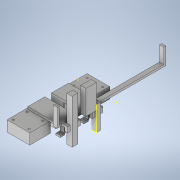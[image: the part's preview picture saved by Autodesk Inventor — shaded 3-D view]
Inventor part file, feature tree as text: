
AUTODESK INVENTOR PART (.ipt)
format: ipt  version: 2020.2 (Build 242310000, 310)  size: 1,098,752 bytes
history: native  units: mm
features: sketch x48, extrude x44, projected_geometry x21, hole x3, plane x1
ambient origin geometry x8: Origin, YZ Plane, XZ Plane, XY Plane, X Axis, Y Axis, Z Axis, Center Point
bodies: Solid1 (feature_tree)
feature tree (117):
  sketch  "Sketch1"  dims[d0=8.0mm d1=98.298mm]
  extrude  "Extrusion1"  Depth=98.298mm
  extrude  "Extrusion2"  Depth=4.0mm
  extrude  "Extrusion3"  Depth=4.0mm TaperAngle=0.0deg
  extrude  "Extrusion4"  Depth=34.0mm
  extrude  "Extrusion5"  Depth=12.7mm
  extrude  "Extrusion6"  Depth=25.0mm
  hole  "Hole1"  [1 undecoded]
  extrude  "Extrusion11"  TaperAngle=60.0deg  [1 undecoded]
  extrude  "Extrusion12"  TaperAngle=120.0deg  [1 undecoded]
  sketch  "Sketch16"  dims[d19=6.4262mm d20=120.0deg]
  extrude  "Extrusion13"  Depth=6.4262mm
  extrude  "Extrusion14"  Depth=6.4262mm
  sketch  "Sketch17"  dims[d21=120.0deg d22=6.4262mm]
  extrude  "Extrusion15"  Depth=25.4mm TaperAngle=0.0deg
  extrude  "Extrusion18"  Depth=12.8016mm
  extrude  "Extrusion19"  Depth=12.8016mm
  extrude  "Extrusion20"  Depth=10.0mm
  hole  "Hole2"  [1 undecoded]
  extrude  "Extrusion21"  Depth=2.0mm
  extrude  "Extrusion22"  Depth=2.0mm
  sketch  "Sketch27"  dims[d45=12.8016mm d46=2.0mm]
  extrude  "Extrusion23"  Depth=25.4mm
  extrude  "Extrusion24"  Depth=32.48mm
  extrude  "Extrusion25"  TaperAngle=90.0deg  [1 undecoded]
  sketch  "Sketch29"  dims[d79=51.53mm d80=32.48mm]
  extrude  "Extrusion26"  Depth=2.0mm
  extrude  "Extrusion27"  Depth=21.0mm
  extrude  "Extrusion28"  Depth=36.0mm TaperAngle=0.0deg
  extrude  "Extrusion29"  Depth=8.0mm
  extrude  "Extrusion30"  Depth=17.5mm
  extrude  "Extrusion32"  Depth=35.0mm
  extrude  "Extrusion38"  Depth=5.0mm
  extrude  "Extrusion39"  TaperAngle=90.0deg  [1 undecoded]
  extrude  "Extrusion40"  Depth=5.0mm
  hole  "Hole4"  [1 undecoded]
  extrude  "Extrusion43"  Depth=1.5mm
  extrude  "Extrusion44"  TaperAngle=0.0deg  [1 undecoded]
  extrude  "Extrusion45"  Depth=28.8036mm
  extrude  "Extrusion46"  Depth=25.4mm
  extrude  "Extrusion47"  TaperAngle=120.0deg  [1 undecoded]
  extrude  "Extrusion48"  Depth=6.4262mm
  extrude  "Extrusion49"  Depth=25.4mm TaperAngle=0.0deg
  extrude  "Extrusion50"  Depth=17.78mm
  sketch  "Sketch56"  dims[d135=3.2131mm d136=6.4262mm]
  extrude  "Extrusion51"  TaperAngle=0.0deg  [1 undecoded]
  sketch  "Sketch58"  dims[d140=8.001mm d141=17.78mm]
  extrude  "Extrusion52"  Depth=10.0mm
  extrude  "Extrusion53"  Depth=5.0mm
  extrude  "Extrusion54"  Depth=51.5366mm
  extrude  "Extrusion55"  Depth=21.0mm
  plane  "Work Plane2"
  extrude  "Extrusion56"  Depth=2.0mm
  extrude  "Extrusion57"  Depth=2.0mm
  sketch  "Sketch65"  dims[d161=2.0mm d162=2.0mm]
  sketch  "Sketch66"  dims[d163=2.0mm d164=2.0mm]
  extrude  "Extrusion58"  Depth=7.0mm
  sketch  "Sketch2"  dims[d2=8.0mm d3=4.0mm]
  sketch  "Sketch3"  dims[d4=4.0mm d5=4.0mm d6=0.0mm]
  sketch  "Sketch4"  dims[d7=34.0mm d8=0.0mm d9=19.558mm]
  sketch  "Sketch5"  dims[d10=16.1125mm d11=12.7mm]
  sketch  "Sketch6"  dims[d12=25.0mm d13=0.0mm d14=7.2009mm]
  sketch  "Sketch14"  dims[d15=6.4135mm d16=12.827mm]
  projected_geometry  "Projected Loop2"
  sketch  "Sketch15"  dims[d17=6.4262mm d18=60.0deg]
  projected_geometry  "Projected Loop3"
  sketch  "Sketch18"  dims[d23=120.0deg d24=6.4262mm]
  sketch  "Sketch21"  dims[d25=120.0deg d26=25.4mm d27=0.0mm]
  sketch  "Sketch22"  dims[d28=6.0mm d29=12.8016mm]
  sketch  "Sketch23"  dims[d30=5.9944mm d31=12.8016mm]
  sketch  "Sketch24"  dims[d32=25.4mm d33=0.0mm d34=10.0mm]
  sketch  "Sketch25"  dims[d35=90.0deg d36=20.0mm]
  projected_geometry  "Projected Loop5"
  sketch  "Sketch26"  dims[d37=3.4mm d38=19.05mm d39=6.2992mm d40=6.35mm d41=90.0deg d42=5.0mm d43=0.0mm d44=2.0mm]
  sketch  "Sketch28"  dims[d47=25.4mm d48=0.0mm d78=16.24mm]
  sketch  "Sketch30"  dims[d81=90.0deg d82=90.0deg]
  sketch  "Sketch32"  dims[d83=4.0mm d84=0.0mm d87=2.0mm]
  projected_geometry  "Projected Loop6"
  sketch  "Sketch33"  dims[d88=2.0mm d89=21.0mm]
  projected_geometry  "Projected Loop7"
  sketch  "Sketch35"  dims[d90=2.0mm d91=36.0mm d92=0.0mm]
  projected_geometry  "Projected Loop8"
  sketch  "Sketch42"  dims[d93=17.78mm d94=8.0mm]
  sketch  "Sketch43"  dims[d95=180.0deg d96=17.5mm]
  projected_geometry  "Projected Loop9"
  projected_geometry  "Projected Loop10"
  projected_geometry  "Projected Loop11"
  projected_geometry  "Projected Loop12"
  sketch  "Sketch44"  dims[d97=90.0deg d98=35.0mm]
  sketch  "Sketch45"  dims[d99=3.5mm d100=5.0mm]
  sketch  "Sketch48"  dims[d101=7.0mm d102=90.0deg]
  sketch  "Sketch49"  dims[d103=5.0mm d104=3.4mm]
  projected_geometry  "Projected Loop13"
  projected_geometry  "Projected Loop14"
  sketch  "Sketch50"  dims[d105=3.4mm d106=25.4mm d107=0.0mm]
  projected_geometry  "Projected Loop15"
  sketch  "Sketch51"  dims[d108=6.4262mm d109=0.0mm d110=1.5mm]
  sketch  "Sketch52"  dims[d111=1.5mm d112=0.0mm d113=0.0mm]
  sketch  "Sketch53"  dims[d128=44.8mm d129=28.8036mm]
  projected_geometry  "Projected Loop16"
  projected_geometry  "Projected Loop17"
  projected_geometry  "Projected Loop18"
  projected_geometry  "Projected Loop19"
  sketch  "Sketch54"  dims[d130=25.4mm d131=0.0mm d132=3.2131mm]
  sketch  "Sketch55"  dims[d133=6.4262mm d134=120.0deg]
  projected_geometry  "Projected Loop20"
  projected_geometry  "Projected Loop21"
  sketch  "Sketch57"  dims[d137=120.0deg d138=25.4mm d139=0.0mm]
  sketch  "Sketch59"  dims[d142=8.001mm d143=0.0mm]
  projected_geometry  "Projected Loop22"
  sketch  "Sketch60"  dims[d144=25.4mm d145=0.0mm d146=10.0mm]
  sketch  "Sketch61"  dims[d147=20.0mm]
  sketch  "Sketch62"  dims[d148=3.4mm d149=19.05mm d150=6.2992mm d151=6.35mm d152=90.0deg d153=5.0mm d154=0.0mm d155=16.2433mm]
  sketch  "Sketch63"  dims[d156=32.4866mm d157=51.5366mm]
  sketch  "Sketch64"  dims[d158=4.0mm d159=0.0mm d160=21.0mm]
  projected_geometry  "Projected Loop23"
  sketch  "Sketch67"  dims[d165=36.0mm d166=0.0mm d167=7.0mm d168=5.0mm d169=5.0mm d170=17.5mm d171=35.0mm d172=3.4mm d173=3.4mm d174=5.0mm d175=0.0mm d176=5.0mm d177=0.0mm d178=1.5mm d179=1.5mm d180=25.4mm d181=0.0mm d182=19.05mm d183=10.0mm d184=5.08mm d185=4.0mm d186=0.0mm d187=10.0mm d188=0.0mm d189=2.0mm d190=3.0mm d191=25.4mm d192=0.0mm d194=30.0mm d195=0.0mm d196=102.489mm d197=0.0mm d201=11.43mm d202=0.0mm d239=25.4mm d240=0.0mm d241=1.5mm d242=0.0mm d243=39.0mm d244=35.0mm d245=39.0mm d246=35.0mm d247=3.0mm d248=0.0mm d249=5.0mm d250=5.0mm d251=29.7mm d252=26.05mm d253=4.0mm d254=4.0mm d255=29.7mm d256=26.05mm d257=3.4mm d258=19.05mm d259=6.2992mm d260=6.35mm d261=90.0deg d262=25.4mm d263=20.594885mm d271=4.0mm d272=28.4mm d273=0.0mm d274=25.4mm d275=0.0mm d276=3.429mm d277=180.0deg d278=30.0mm d279=0.0mm d280=6.35mm d281=25.4mm d282=0.0mm d283=5.08mm d284=25.4mm d285=0.0mm d286=2.0mm d287=0.0mm d288=12.7mm d289=0.0mm d290=2.0mm d291=42.9956mm d292=37.0012mm d293=37.0012mm d294=2.0mm d295=2.0mm d296=20.0mm d297=0.0mm d298=15.0086mm d299=2.0mm d300=27.4mm d301=90.0deg d302=5.0mm d303=10.0mm d304=10.0mm d305=83.2mm d306=3.302mm d307=12.0mm d308=0.0mm d309=1.0mm d310=0.0mm d311=5.08mm d312=90.0deg d313=25.4mm d314=0.0mm d315=5.08mm d316=25.4mm d317=0.0mm d318=5.08mm d319=25.4mm d320=0.0mm d321=5.08mm d322=25.4mm d323=0.0mm d324=26.2mm d325=5.0mm d326=46.2mm d327=3.302mm d328=8.0mm d329=0.0mm d331=9.0mm d332=10.0mm d333=45.8mm d334=20.0mm d335=0.0mm d214=12.7mm d215=0.872665mm d216=12.7mm d217=0.872665mm d228=12.7mm d229=0.872665mm d230=12.7mm d231=0.872665mm d330=12.7mm]
note: 10 required parameter values undecoded (feature->parameter linkage not recoverable at this tier; creation-order binding heuristic only, values carry confidence <= 0.55)
